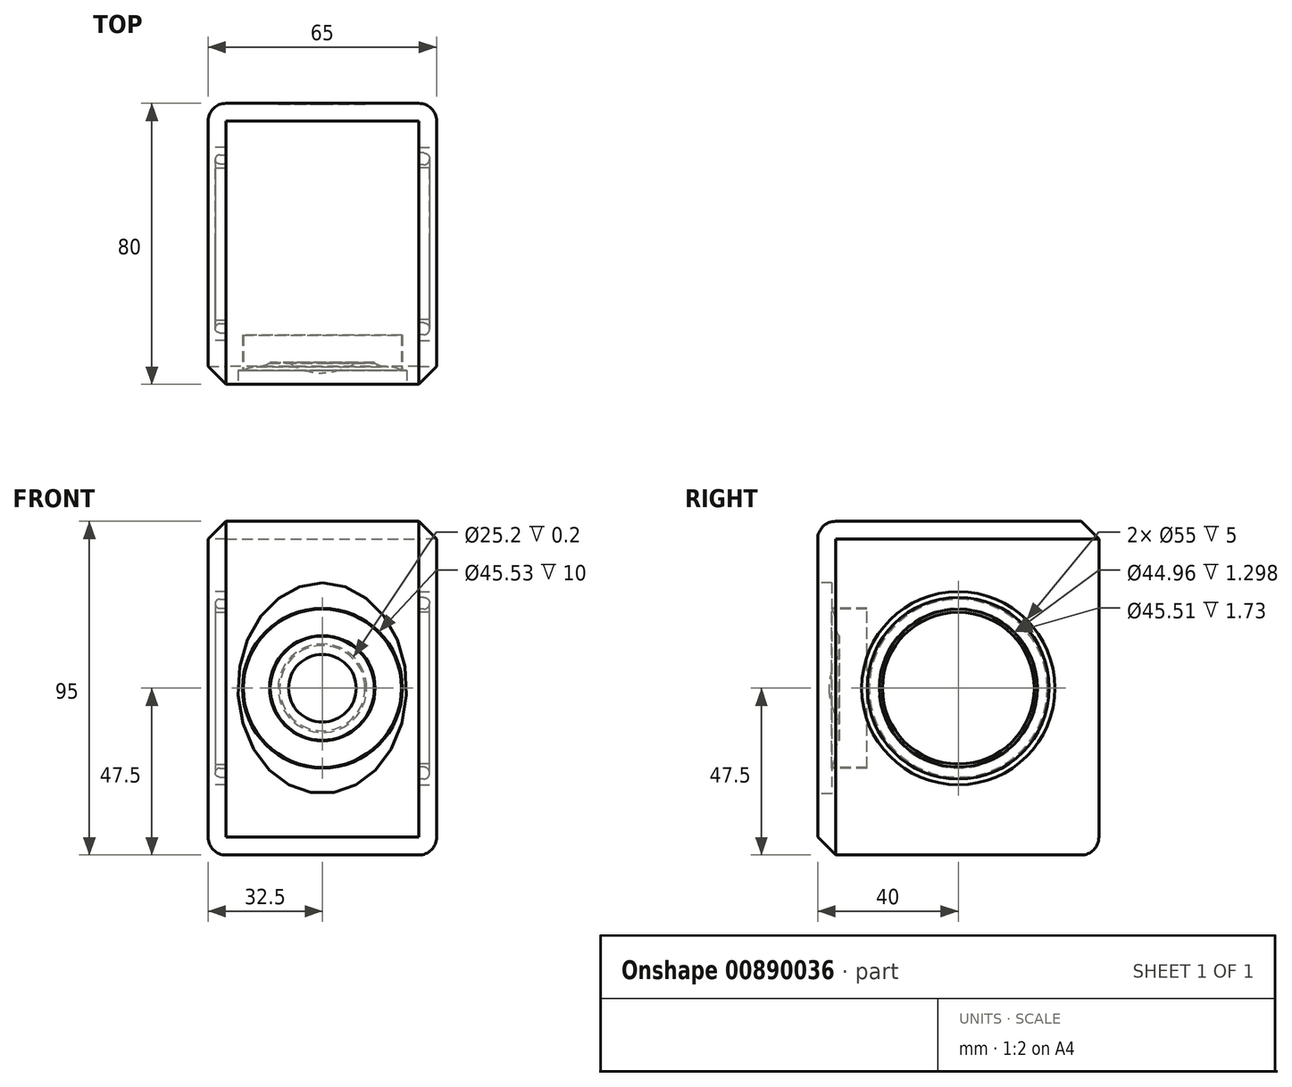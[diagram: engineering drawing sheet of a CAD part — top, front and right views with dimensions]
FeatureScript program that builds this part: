
annotation { "Feature Type Name" : "Feature", "Feature Type Description" : "" }
export const myFeature = defineFeature(function(context is Context, id is Id, definition is map)
    precondition{}
    {
        {
            var Q0;
            Q0=qCreatedBy(makeId("Front.planeOp"),FACE);
            var sketch = newSketch(context, id + "F0", { "sketchPlane" : qUnion([Q0])});
            skLineSegment(sketch, "E0.bottom", {"start": v(-32.5, 47.5) * mm, "end": v(32.5, 47.5) * mm});
            skLineSegment(sketch, "E0.top", {"start": v(-32.5, -47.5) * mm, "end": v(32.5, -47.5) * mm});
            skLineSegment(sketch, "E0.left", {"start": v(-32.5, 47.5) * mm, "end": v(-32.5, -47.5) * mm});
            skLineSegment(sketch, "E0.right", {"start": v(32.5, 47.5) * mm, "end": v(32.5, -47.5) * mm});
            skPoint(sketch, "E0.middle", {"position": v(0, 0) * mm});
            skSolve(sketch);
        }
        {
            var Q0;
            Q0 = qSketchRegion(id + "F0", true);
            extrude(context, id + "F1", {"entities" : qUnion([Q0]), "depth" : 40 * mm, "offsetDistance" : 25.4 * mm});
        }
        {
            var Q0;
            Q0=makeQuery(id+"F1.opExtrude","CAP_FACE",FACE,{"disambiguationData":[OSD([sQuery(id+"F0.wireOp",EDGE,"E0.bottom"),sQuery(id+"F0.wireOp",EDGE,"E0.top"),sQuery(id+"F0.wireOp",EDGE,"E0.left"),sQuery(id+"F0.wireOp",EDGE,"E0.right")])],"isStart":true});
            extrude(context, id + "F2", {"entities" : qUnion([Q0]), "operationType" : NewBodyOperationType.ADD, "depth" : 40 * mm, "offsetDistance" : 25.4 * mm});
        }
        {
            var Q0;
            {var subQ0=sQuery(id+"F0.wireOp",EDGE,"E0.left");Q0=makeQuery(id+"F2.boolean.opBoolean","MERGE",FACE,{"derivedFrom":[makeQuery(id+"F1.opExtrude","SWEPT_FACE",FACE,{"disambiguationData":[OSD([subQ0])]}),makeQuery(id+"F2.opExtrude","SWEPT_FACE",FACE,{"disambiguationData":[OSD([subQ0])]})]});}
            var sketch = newSketch(context, id + "F3", { "sketchPlane" : qUnion([Q0])});
            skCircle(sketch, "E1", {"center": v(0, 0) * mm, "radius": 27.5 * mm});
            skSolve(sketch);
        }
        {
            var Q0;
            {var subQ0=sQuery(id+"F0.wireOp",EDGE,"E0.right");Q0=makeQuery(id+"F2.boolean.opBoolean","MERGE",FACE,{"derivedFrom":[makeQuery(id+"F1.opExtrude","SWEPT_FACE",FACE,{"disambiguationData":[OSD([subQ0])]}),makeQuery(id+"F2.opExtrude","SWEPT_FACE",FACE,{"disambiguationData":[OSD([subQ0])]})]});}
            var sketch = newSketch(context, id + "F4", { "sketchPlane" : qUnion([Q0])});
            skCircle(sketch, "E2", {"center": v(0, 0) * mm, "radius": 27.5 * mm});
            skSolve(sketch);
        }
        {
            var Q0;
            Q0=makeQuery(id+"F4.imprint","IMPRINT",FACE,{"disambiguationData":[TD([[makeQuery(id+"F4.imprint","IMPRINT",EDGE,{"derivedFrom":sQuery(id+"F4.wireOp",EDGE,"E2")}),1.0]])]});
            extrude(context, id + "F5", {"entities" : qUnion([Q0]), "operationType" : NewBodyOperationType.REMOVE, "oppositeDirection" : true, "depth" : 5 * mm, "offsetDistance" : 25.4 * mm});
        }
        {
            var Q0;
            Q0=makeQuery(id+"F3.imprint","IMPRINT",FACE,{"disambiguationData":[TD([[makeQuery(id+"F3.imprint","IMPRINT",EDGE,{"derivedFrom":sQuery(id+"F3.wireOp",EDGE,"E1")}),1.0]])]});
            extrude(context, id + "F6", {"entities" : qUnion([Q0]), "operationType" : NewBodyOperationType.REMOVE, "oppositeDirection" : true, "depth" : 5 * mm, "offsetDistance" : 25.4 * mm});
        }
        {
            var Q0;
            Q0=makeQuery(id+"F6.boolean.opBoolean","COPY",FACE,{"derivedFrom":makeQuery(id+"F6.opExtrude","CAP_FACE",FACE,{"disambiguationData":[OSD([sQuery(id+"F3.wireOp",EDGE,"E1")])],"isStart":false})});
            var sketch = newSketch(context, id + "F7", { "sketchPlane" : qUnion([Q0])});
            skCircle(sketch, "E3", {"center": v(0, 0) * mm, "radius": 25.3 * mm});
            skSolve(sketch);
        }
        {
            var Q0;
            Q0=makeQuery(id+"F5.boolean.opBoolean","COPY",FACE,{"derivedFrom":makeQuery(id+"F5.opExtrude","CAP_FACE",FACE,{"disambiguationData":[OSD([sQuery(id+"F4.wireOp",EDGE,"E2")])],"isStart":false})});
            var sketch = newSketch(context, id + "F8", { "sketchPlane" : qUnion([Q0])});
            skCircle(sketch, "E4", {"center": v(0, 0) * mm, "radius": 25.88 * mm});
            skSolve(sketch);
        }
        {
            var Q0;
            Q0=makeQuery(id+"F8.imprint","IMPRINT",FACE,{"disambiguationData":[TD([[makeQuery(id+"F8.imprint","IMPRINT",EDGE,{"derivedFrom":sQuery(id+"F8.wireOp",EDGE,"E4")}),1.0]])]});
            var sketch = newSketch(context, id + "F9", { "sketchPlane" : qUnion([Q0])});
            skCircle(sketch, "E5", {"center": v(0, 0) * mm, "radius": 22.48 * mm});
            skSolve(sketch);
        }
        {
            var Q0;
            Q0=makeQuery(id+"F9.imprint","IMPRINT",FACE,{"disambiguationData":[TD([[makeQuery(id+"F9.imprint","IMPRINT",EDGE,{"derivedFrom":sQuery(id+"F9.wireOp",EDGE,"E5")}),1.0]])]});
            var sketch = newSketch(context, id + "F10", { "sketchPlane" : qUnion([Q0])});
            skCircle(sketch, "E6", {"center": v(0, 0) * mm, "radius": 21.59 * mm});
            skSolve(sketch);
        }
        {
            var Q0;
            Q0=makeQuery(id+"F9.imprint","IMPRINT",FACE,{"disambiguationData":[TD([[makeQuery(id+"F9.imprint","IMPRINT",EDGE,{"derivedFrom":sQuery(id+"F9.wireOp",EDGE,"E5")}),-1.0]])]});
            extrude(context, id + "F11", {"entities" : qUnion([Q0]), "operationType" : NewBodyOperationType.ADD, "depth" : 3 * mm, "offsetDistance" : 25.4 * mm});
        }
        {
            var Q0;
            Q0=makeQuery(id+"F10.imprint","IMPRINT",FACE,{"disambiguationData":[TD([[makeQuery(id+"F10.imprint","IMPRINT",EDGE,{"derivedFrom":sQuery(id+"F10.wireOp",EDGE,"E6")}),1.0]])]});
            extrude(context, id + "F12", {"entities" : qUnion([Q0]), "operationType" : NewBodyOperationType.ADD, "depth" : 3 * mm, "offsetDistance" : 25.4 * mm});
        }
        {
            var Q0;
            Q0=makeQuery(id+"F11.opExtrude","CAP_FACE",FACE,{"disambiguationData":[OSD([sQuery(id+"F8.wireOp",EDGE,"E4"),sQuery(id+"F9.wireOp",EDGE,"E5")])],"isStart":false});
            fillet(context, id + "F13", {"entities" : qUnion([Q0]), "radius" : 1.7 * mm, "tangentPropagation" : true, "allowEdgeOverflow" : false});
        }
        {
            var Q0;
            Q0=makeQuery(id+"F7.imprint","IMPRINT",FACE,{"disambiguationData":[TD([[makeQuery(id+"F7.imprint","IMPRINT",EDGE,{"derivedFrom":sQuery(id+"F7.wireOp",EDGE,"E3")}),1.0]])]});
            var sketch = newSketch(context, id + "F14", { "sketchPlane" : qUnion([Q0])});
            skSolve(sketch);
        }
        {
            var Q0;
            Q0=makeQuery(id+"F14.imprint","IMPRINT",FACE,{"disambiguationData":[TD([[makeQuery(id+"F14.imprint","IMPRINT",EDGE,{"derivedFrom":makeQuery(id+"F7.imprint","IMPRINT",EDGE,{"derivedFrom":sQuery(id+"F7.wireOp",EDGE,"E3")})}),1.0]])]});
            var sketch = newSketch(context, id + "F15", { "sketchPlane" : qUnion([Q0])});
            skCircle(sketch, "E7", {"center": v(0, 0) * mm, "radius": 22.75 * mm});
            skSolve(sketch);
        }
        {
            var Q0;
            Q0=makeQuery(id+"F15.imprint","IMPRINT",FACE,{"disambiguationData":[TD([[makeQuery(id+"F15.imprint","IMPRINT",EDGE,{"derivedFrom":sQuery(id+"F15.wireOp",EDGE,"E7")}),1.0]])]});
            var sketch = newSketch(context, id + "F16", { "sketchPlane" : qUnion([Q0])});
            skCircle(sketch, "E8", {"center": v(0, 0) * mm, "radius": 21.69 * mm});
            skSolve(sketch);
        }
        {
            var Q0;
            Q0=makeQuery(id+"F15.imprint","IMPRINT",FACE,{"disambiguationData":[TD([[makeQuery(id+"F15.imprint","IMPRINT",EDGE,{"derivedFrom":sQuery(id+"F15.wireOp",EDGE,"E7")}),-1.0]])]});
            extrude(context, id + "F17", {"entities" : qUnion([Q0]), "operationType" : NewBodyOperationType.ADD, "depth" : 3 * mm, "offsetDistance" : 25.4 * mm});
        }
        {
            var Q0;
            Q0=makeQuery(id+"F16.imprint","IMPRINT",FACE,{"disambiguationData":[TD([[makeQuery(id+"F16.imprint","IMPRINT",EDGE,{"derivedFrom":sQuery(id+"F16.wireOp",EDGE,"E8")}),1.0]])]});
            extrude(context, id + "F18", {"entities" : qUnion([Q0]), "operationType" : NewBodyOperationType.ADD, "depth" : 3 * mm, "offsetDistance" : 25.4 * mm});
        }
        {
            var Q0;
            Q0=makeQuery(id+"F2.opExtrude","CAP_FACE",FACE,{"disambiguationData":[OSD([sQuery(id+"F0.wireOp",EDGE,"E0.bottom"),sQuery(id+"F0.wireOp",EDGE,"E0.top"),sQuery(id+"F0.wireOp",EDGE,"E0.left"),sQuery(id+"F0.wireOp",EDGE,"E0.right")])],"isStart":false});
            var sketch = newSketch(context, id + "F19", { "sketchPlane" : qUnion([Q0])});
            skCircle(sketch, "E9", {"center": v(0, 0) * mm, "radius": 12.6 * mm});
            skCircle(sketch, "E10", {"center": v(0, 0) * mm, "radius": 12.13 * mm});
            skSolve(sketch);
        }
        {
            var Q0;
            Q0=makeQuery(id+"F19.imprint","IMPRINT",FACE,{"disambiguationData":[TD([[makeQuery(id+"F19.imprint","IMPRINT",EDGE,{"derivedFrom":sQuery(id+"F19.wireOp",EDGE,"E9")}),1.0]])]});
            extrude(context, id + "F20", {"entities" : qUnion([Q0]), "operationType" : NewBodyOperationType.REMOVE, "oppositeDirection" : true, "depth" : .2 * mm, "offsetDistance" : 25.4 * mm});
        }
        {
            var Q0;
            Q0=makeQuery(id+"F16.imprint","IMPRINT",FACE,{"disambiguationData":[TD([[makeQuery(id+"F16.imprint","IMPRINT",EDGE,{"derivedFrom":sQuery(id+"F16.wireOp",EDGE,"E8")}),1.0]])]});
            extrude(context, id + "F21", {"entities" : qUnion([Q0]), "operationType" : NewBodyOperationType.ADD, "depth" : 3 * mm, "offsetDistance" : 25.4 * mm});
        }
        {
            var Q0;
            Q0=makeQuery(id+"F1.opExtrude","CAP_FACE",FACE,{"disambiguationData":[OSD([sQuery(id+"F0.wireOp",EDGE,"E0.bottom"),sQuery(id+"F0.wireOp",EDGE,"E0.top"),sQuery(id+"F0.wireOp",EDGE,"E0.left"),sQuery(id+"F0.wireOp",EDGE,"E0.right")])],"isStart":false});
            var sketch = newSketch(context, id + "F22", { "sketchPlane" : qUnion([Q0])});
            skCircle(sketch, "E11", {"center": v(0, 0) * mm, "radius": 22.5 * mm});
            skSolve(sketch);
        }
        {
            var Q0;
            Q0=makeQuery(id+"F22.imprint","IMPRINT",FACE,{"disambiguationData":[TD([[makeQuery(id+"F22.imprint","IMPRINT",EDGE,{"derivedFrom":sQuery(id+"F22.wireOp",EDGE,"E11")}),1.0]])]});
            extrude(context, id + "F23", {"entities" : qUnion([Q0]), "operationType" : NewBodyOperationType.REMOVE, "oppositeDirection" : true, "depth" : 5 * mm, "offsetDistance" : 25.4 * mm});
        }
        {
            var Q0;
            Q0=makeQuery(id+"F23.boolean.opBoolean","COPY",FACE,{"derivedFrom":makeQuery(id+"F23.opExtrude","CAP_FACE",FACE,{"disambiguationData":[OSD([sQuery(id+"F22.wireOp",EDGE,"E11")])],"isStart":false})});
            var sketch = newSketch(context, id + "F24", { "sketchPlane" : qUnion([Q0])});
            skCircle(sketch, "E12", {"center": v(0, 0) * mm, "radius": 20 * mm});
            skSolve(sketch);
        }
        {
            var Q0;
            Q0=makeQuery(id+"F24.imprint","IMPRINT",FACE,{"disambiguationData":[TD([[makeQuery(id+"F24.imprint","IMPRINT",EDGE,{"derivedFrom":sQuery(id+"F24.wireOp",EDGE,"E12")}),1.0]])]});
            extrude(context, id + "F25", {"entities" : qUnion([Q0]), "operationType" : NewBodyOperationType.REMOVE, "oppositeDirection" : true, "depth" : 1 * mm, "offsetDistance" : 25.4 * mm});
        }
        {
            var Q0;
            Q0=makeQuery(id+"F25.boolean.opBoolean","COPY",FACE,{"derivedFrom":makeQuery(id+"F25.opExtrude","CAP_FACE",FACE,{"disambiguationData":[OSD([sQuery(id+"F24.wireOp",EDGE,"E12")])],"isStart":false})});
            var sketch = newSketch(context, id + "F26", { "sketchPlane" : qUnion([Q0])});
            skCircle(sketch, "E13", {"center": v(0, 0) * mm, "radius": 10 * mm});
            skSolve(sketch);
        }
        {
            var Q0;
            Q0=makeQuery(id+"F26.imprint","IMPRINT",FACE,{"disambiguationData":[TD([[makeQuery(id+"F26.imprint","IMPRINT",EDGE,{"derivedFrom":sQuery(id+"F26.wireOp",EDGE,"E13")}),1.0]])]});
            extrude(context, id + "F27", {"entities" : qUnion([Q0]), "operationType" : NewBodyOperationType.REMOVE, "oppositeDirection" : true, "depth" : .2 * mm, "offsetDistance" : 25.4 * mm});
        }
        {
            var Q0;
            Q0=makeQuery(id+"F27.boolean.opBoolean","COPY",FACE,{"derivedFrom":makeQuery(id+"F27.opExtrude","CAP_FACE",FACE,{"disambiguationData":[OSD([sQuery(id+"F26.wireOp",EDGE,"E13")])],"isStart":false})});
            var sketch = newSketch(context, id + "F28", { "sketchPlane" : qUnion([Q0])});
            skCircle(sketch, "E14", {"center": v(0, 0) * mm, "radius": 9.62 * mm});
            skSolve(sketch);
        }
        {
            var Q0;
            Q0 = qSketchRegion(id + "F28", true);
            extrude(context, id + "F29", {"entities" : qUnion([Q0]), "operationType" : NewBodyOperationType.ADD, "depth" : 3 * mm, "offsetDistance" : 25.4 * mm});
        }
        {
            var Q0;
            Q0=makeQuery(id+"F29.opExtrude","CAP_FACE",FACE,{"disambiguationData":[OSD([sQuery(id+"F28.wireOp",EDGE,"E14")])],"isStart":false});
            fillet(context, id + "F30", {"entities" : qUnion([Q0]), "radius" : 16.9 * mm, "tangentPropagation" : true, "allowEdgeOverflow" : false});
        }
        {
            var Q0;
            Q0=makeQuery(id+"F1.opExtrude","CAP_EDGE",EDGE,{"disambiguationData":[OSD([sQuery(id+"F0.wireOp",EDGE,"E0.bottom")])],"isStart":false});
            var Q1;
            Q1=makeQuery(id+"F2.opExtrude","CAP_EDGE",EDGE,{"disambiguationData":[OSD([sQuery(id+"F0.wireOp",EDGE,"E0.top")])],"isStart":false});
            var Q2;
            Q2=makeQuery(id+"F2.opExtrude","CAP_EDGE",EDGE,{"disambiguationData":[OSD([sQuery(id+"F0.wireOp",EDGE,"E0.right")])],"isStart":false});
            var Q3;
            Q3=makeQuery(id+"F2.opExtrude","CAP_EDGE",EDGE,{"disambiguationData":[OSD([sQuery(id+"F0.wireOp",EDGE,"E0.left")])],"isStart":false});
            var Q4;
            {var subQ0=sQuery(id+"F0.wireOp",EDGE,"E0.left");var subQ1=sQuery(id+"F0.wireOp",EDGE,"E0.top");Q4=makeQuery(id+"F2.boolean.opBoolean","MERGE",EDGE,{"derivedFrom":[makeQuery(id+"F1.opExtrude","SWEPT_EDGE",EDGE,{"disambiguationData":[OSD([subQ1,subQ0])]}),makeQuery(id+"F2.opExtrude","SWEPT_EDGE",EDGE,{"disambiguationData":[OSD([subQ1,subQ0])]})]});}
            var Q5;
            {var subQ0=sQuery(id+"F0.wireOp",EDGE,"E0.right");var subQ1=sQuery(id+"F0.wireOp",EDGE,"E0.top");Q5=makeQuery(id+"F2.boolean.opBoolean","MERGE",EDGE,{"derivedFrom":[makeQuery(id+"F1.opExtrude","SWEPT_EDGE",EDGE,{"disambiguationData":[OSD([subQ1,subQ0])]}),makeQuery(id+"F2.opExtrude","SWEPT_EDGE",EDGE,{"disambiguationData":[OSD([subQ1,subQ0])]})]});}
            fillet(context, id + "F31", {"entities" : qUnion([Q0, Q1, Q2, Q3, Q4, Q5]), "radius" : 5.08 * mm, "tangentPropagation" : true, "allowEdgeOverflow" : false});
        }
        {
            var Q0;
            {var subQ0=sQuery(id+"F0.wireOp",EDGE,"E0.right");var subQ1=sQuery(id+"F0.wireOp",EDGE,"E0.bottom");Q0=makeQuery(id+"F2.boolean.opBoolean","MERGE",EDGE,{"derivedFrom":[makeQuery(id+"F1.opExtrude","SWEPT_EDGE",EDGE,{"disambiguationData":[OSD([subQ1,subQ0])]}),makeQuery(id+"F2.opExtrude","SWEPT_EDGE",EDGE,{"disambiguationData":[OSD([subQ1,subQ0])]})]});}
            var Q1;
            Q1=makeQuery(id+"F2.opExtrude","CAP_EDGE",EDGE,{"disambiguationData":[OSD([sQuery(id+"F0.wireOp",EDGE,"E0.bottom")])],"isStart":false});
            var Q2;
            {var subQ0=sQuery(id+"F0.wireOp",EDGE,"E0.left");var subQ1=sQuery(id+"F0.wireOp",EDGE,"E0.bottom");Q2=makeQuery(id+"F2.boolean.opBoolean","MERGE",EDGE,{"derivedFrom":[makeQuery(id+"F1.opExtrude","SWEPT_EDGE",EDGE,{"disambiguationData":[OSD([subQ1,subQ0])]}),makeQuery(id+"F2.opExtrude","SWEPT_EDGE",EDGE,{"disambiguationData":[OSD([subQ1,subQ0])]})]});}
            var Q3;
            Q3=makeQuery(id+"F1.opExtrude","CAP_EDGE",EDGE,{"disambiguationData":[OSD([sQuery(id+"F0.wireOp",EDGE,"E0.left")])],"isStart":false});
            var Q4;
            Q4=makeQuery(id+"F1.opExtrude","CAP_EDGE",EDGE,{"disambiguationData":[OSD([sQuery(id+"F0.wireOp",EDGE,"E0.right")])],"isStart":false});
            chamfer(context, id + "F32", {"entities" : qUnion([Q0, Q1, Q2, Q3, Q4]), "width" : 5.08 * mm, "tangentPropagation" : true});
        }
        {
            var Q0;
            Q0=makeQuery(id+"F17.opExtrude","CAP_FACE",FACE,{"disambiguationData":[OSD([sQuery(id+"F7.wireOp",EDGE,"E3"),sQuery(id+"F15.wireOp",EDGE,"E7")])],"isStart":false});
            fillet(context, id + "F33", {"entities" : qUnion([Q0]), "radius" : 1.27 * mm, "tangentPropagation" : true, "allowEdgeOverflow" : false});
        }
        {
            var Q0;
            Q0=makeQuery(id+"F1.opExtrude","CAP_FACE",FACE,{"disambiguationData":[OSD([sQuery(id+"F0.wireOp",EDGE,"E0.bottom"),sQuery(id+"F0.wireOp",EDGE,"E0.top"),sQuery(id+"F0.wireOp",EDGE,"E0.left"),sQuery(id+"F0.wireOp",EDGE,"E0.right")])],"isStart":false});
            var sketch = newSketch(context, id + "F34", { "sketchPlane" : qUnion([Q0])});
            skEllipse(sketch, "E15", {"center": v(0, 0) * mm, "majorRadius": 30 * mm, "minorRadius": 24 * mm, "majorAxis": v(0, 1)});
            skSolve(sketch);
        }
        {
            var Q0;
            Q0=makeQuery(id+"F34.imprint","IMPRINT",FACE,{"disambiguationData":[TD([[makeQuery(id+"F34.imprint","IMPRINT",EDGE,{"derivedFrom":sQuery(id+"F34.wireOp",EDGE,"E15")}),1.0]])]});
            extrude(context, id + "F35", {"entities" : qUnion([Q0]), "operationType" : NewBodyOperationType.REMOVE, "oppositeDirection" : true, "depth" : 4 * mm, "offsetDistance" : 25.4 * mm});
        }
        {
            var Q0;
            Q0=makeQuery(id+"F25.boolean.opBoolean","COPY",FACE,{"derivedFrom":makeQuery(id+"F25.opExtrude","CAP_FACE",FACE,{"disambiguationData":[OSD([sQuery(id+"F24.wireOp",EDGE,"E12")])],"isStart":false})});
            chamfer(context, id + "F36", {"entities" : qUnion([Q0]), "width" : 5 * mm, "tangentPropagation" : true});
        }
        {
            var Q0;
            Q0=makeQuery(id+"F23.boolean.opBoolean","COPY",FACE,{"derivedFrom":makeQuery(id+"F23.opExtrude","CAP_FACE",FACE,{"disambiguationData":[OSD([sQuery(id+"F22.wireOp",EDGE,"E11")])],"isStart":false})});
            fillet(context, id + "F37", {"entities" : qUnion([Q0]), "radius" : 7.52 * mm, "tangentPropagation" : true, "allowEdgeOverflow" : false});
        }
        {
            var Q0;
            Q0=makeQuery(id+"F35.boolean.opBoolean","COPY",FACE,{"derivedFrom":makeQuery(id+"F35.opExtrude","CAP_FACE",FACE,{"disambiguationData":[OSD([sQuery(id+"F22.wireOp",EDGE,"E11"),sQuery(id+"F34.wireOp",EDGE,"E15")])],"isStart":false})});
            var sketch = newSketch(context, id + "F38", { "sketchPlane" : qUnion([Q0])});
            skCircle(sketch, "E16", {"center": v(0, 0) * mm, "radius": 22.77 * mm});
            skSolve(sketch);
        }
        {
            var Q0;
            Q0=makeQuery(id+"F38.imprint","IMPRINT",FACE,{"disambiguationData":[TD([[makeQuery(id+"F38.imprint","IMPRINT",EDGE,{"derivedFrom":sQuery(id+"F38.wireOp",EDGE,"E16")}),1.0]])]});
            extrude(context, id + "F39", {"entities" : qUnion([Q0]), "operationType" : NewBodyOperationType.REMOVE, "surfaceOperationType" : NewSurfaceOperationType.ADD, "oppositeDirection" : true, "depth" : 10 * mm, "offsetDistance" : 25.4 * mm});
        }
    });
